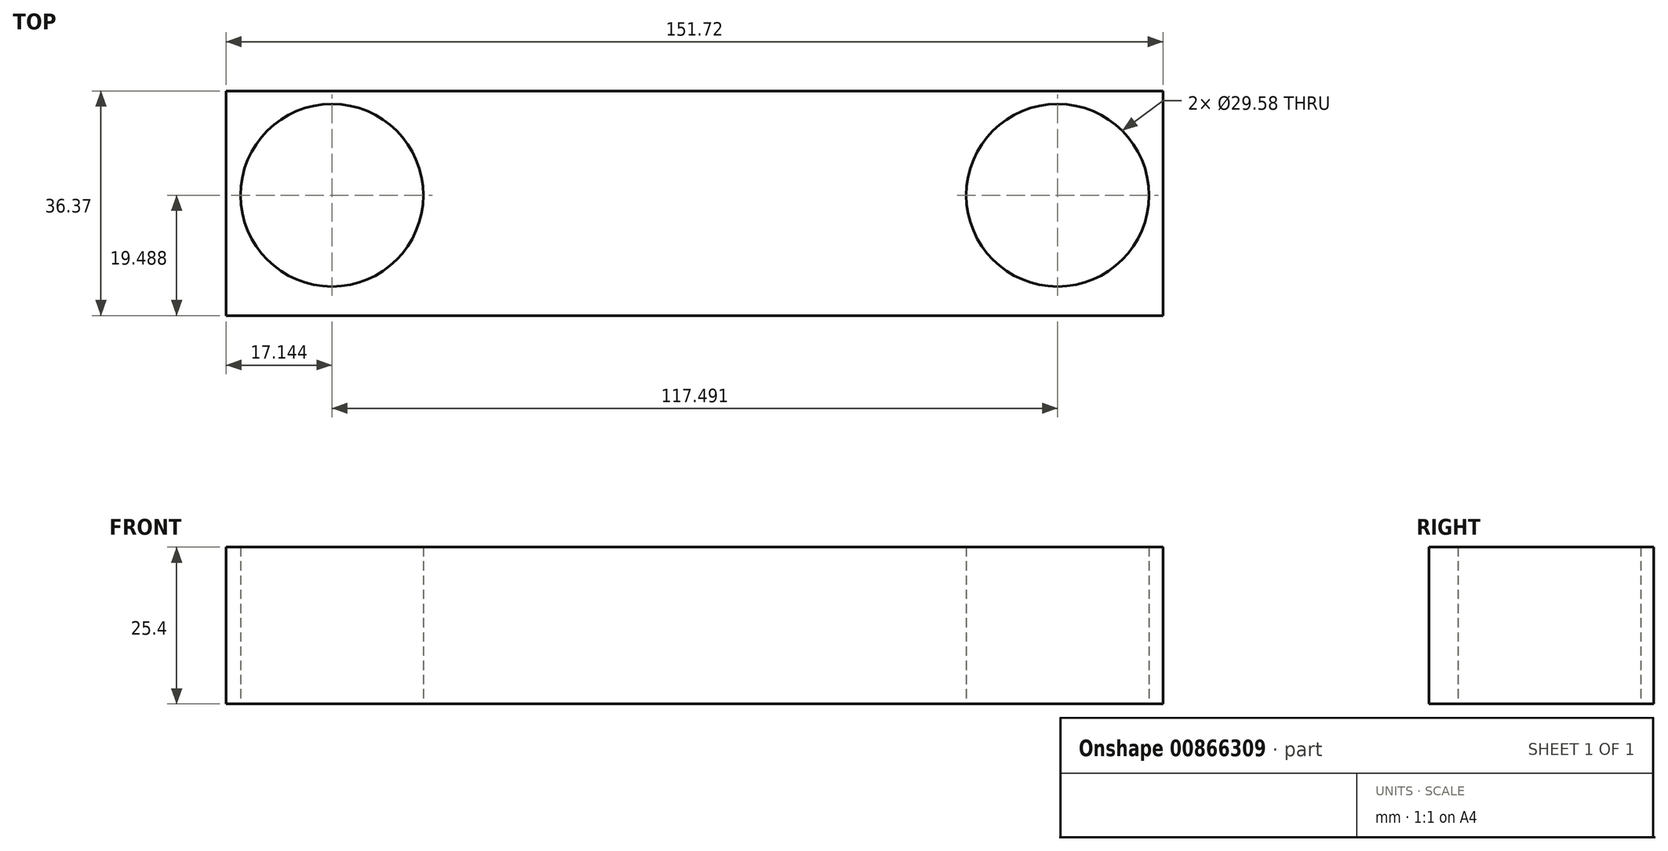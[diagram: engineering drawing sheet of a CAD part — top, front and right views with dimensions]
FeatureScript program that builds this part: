
annotation { "Feature Type Name" : "Feature", "Feature Type Description" : "" }
export const myFeature = defineFeature(function(context is Context, id is Id, definition is map)
    precondition{}
    {
        {
            var Q0;
            Q0=qCreatedBy(makeId("Top.planeOp"),FACE);
            var sketch = newSketch(context, id + "F0", { "sketchPlane" : qUnion([Q0])});
            skLineSegment(sketch, "E0.bottom", {"start": v(-75.9, 59.92) * mm, "end": v(75.83, 59.92) * mm});
            skLineSegment(sketch, "E0.top", {"start": v(-75.9, 23.55) * mm, "end": v(75.83, 23.55) * mm});
            skLineSegment(sketch, "E0.left", {"start": v(-75.9, 59.92) * mm, "end": v(-75.9, 23.55) * mm});
            skLineSegment(sketch, "E0.right", {"start": v(75.83, 59.92) * mm, "end": v(75.83, 23.55) * mm});
            skCircle(sketch, "E1", {"center": v(-58.75, 43.04) * mm, "radius": 14.79 * mm});
            skCircle(sketch, "E2.MirrorC", {"center": v(58.75, 43.04) * mm, "radius": 14.79 * mm});
            skSolve(sketch);
        }
        {
            var Q0;
            Q0=qSketchRegion(id+"F1NKy7udbwcnx6w_0",true);
            var Q1;
            Q1=qSketchRegion(id+"F0",true);
            extrude(context, id + "F1", {"entities" : qUnion([Q0, Q1]), "depth" : 25.4 * mm, "offsetDistance" : 25.4 * mm});
        }
    });
